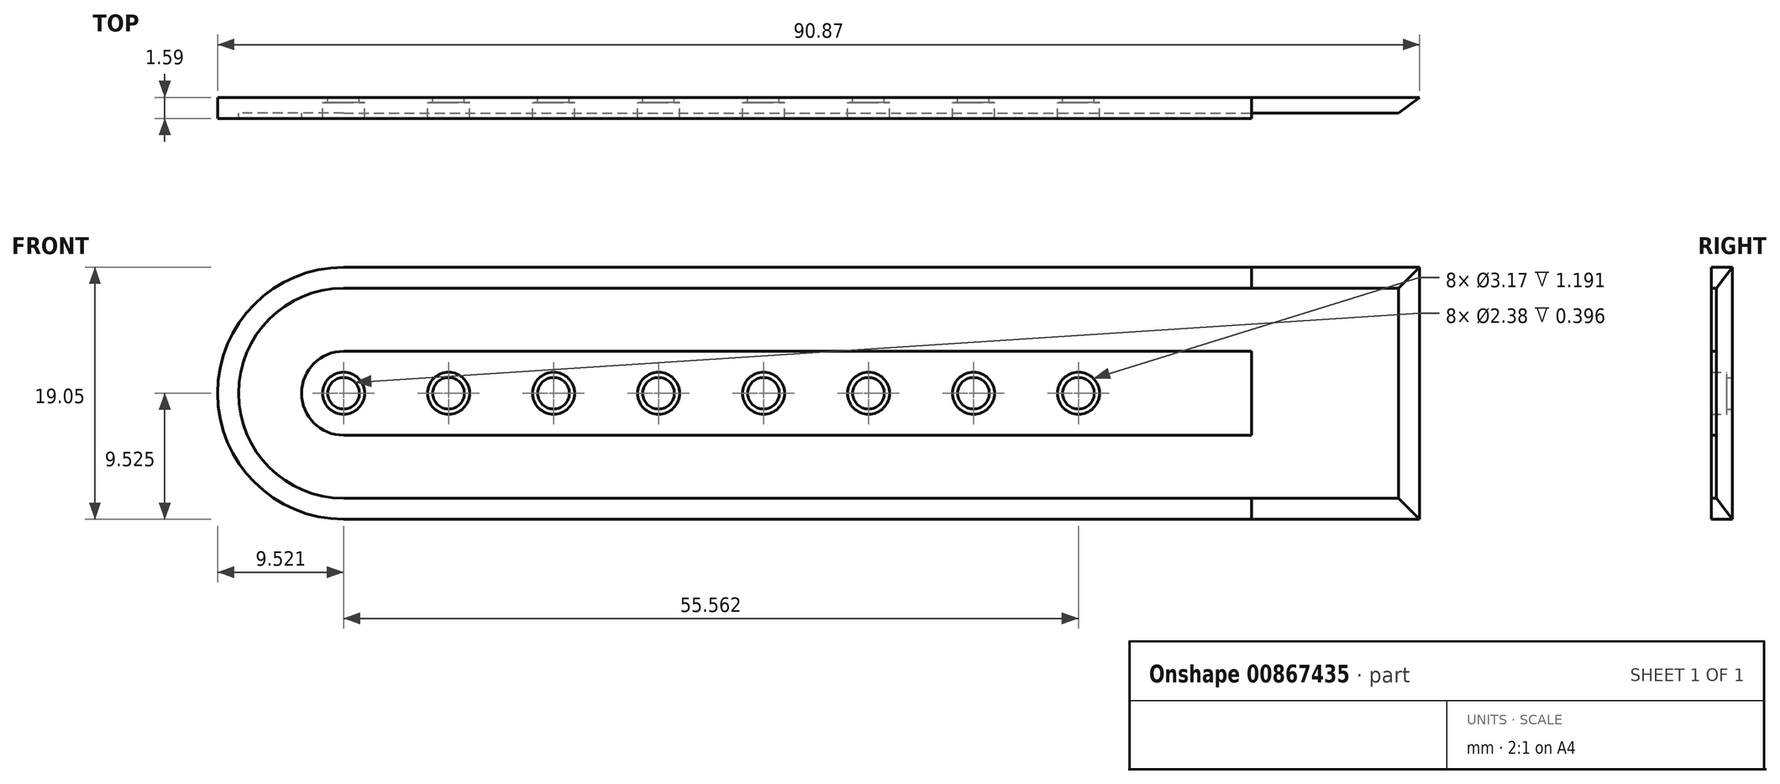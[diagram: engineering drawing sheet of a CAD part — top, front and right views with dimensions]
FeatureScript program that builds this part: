
annotation { "Feature Type Name" : "Feature", "Feature Type Description" : "" }
export const myFeature = defineFeature(function(context is Context, id is Id, definition is map)
    precondition{}
    {
        {
            var Q0;
            Q0=qCreatedBy(makeId("Front.planeOp"),FACE);
            var sketch = newSketch(context, id + "F0", { "sketchPlane" : qUnion([Q0])});
            skLineSegment(sketch, "E0", {"start": v(0, 0) * mm, "end": v(-81.36, 0) * mm});
            skLineSegment(sketch, "E1", {"start": v(0, 19.05) * mm, "end": v(-81.36, 19.05) * mm});
            skArc(sketch, "E2", {"start": v(-81.36, 19.05) * mm, "mid": v(-90.88, 9.52) * mm, "end": v(-81.36, 0) * mm});
            skLineSegment(sketch, "E3", {"start": v(0, 19.05) * mm, "end": v(0, 0) * mm});
            skCircle(sketch, "E4", {"center": v(-73.42, 9.52) * mm, "radius": 1.59 * mm});
            skCircle(sketch, "E5", {"center": v(-65.48, 9.52) * mm, "radius": 1.59 * mm});
            skCircle(sketch, "E6", {"center": v(-57.55, 9.52) * mm, "radius": 1.59 * mm});
            skCircle(sketch, "E7", {"center": v(-49.6, 9.52) * mm, "radius": 1.59 * mm});
            skCircle(sketch, "E8", {"center": v(-41.67, 9.52) * mm, "radius": 1.59 * mm});
            skCircle(sketch, "E9", {"center": v(-33.73, 9.52) * mm, "radius": 1.59 * mm});
            skCircle(sketch, "E10", {"center": v(-81.36, 9.52) * mm, "radius": 1.59 * mm});
            skCircle(sketch, "E11", {"center": v(-25.8, 9.52) * mm, "radius": 1.59 * mm});
            skArc(sketch, "E12", {"start": v(-81.36, 17.46) * mm, "mid": v(-89.3, 9.52) * mm, "end": v(-81.36, 1.59) * mm});
            skCircle(sketch, "E13", {"center": v(-81.36, 9.52) * mm, "radius": 1.2 * mm});
            skCircle(sketch, "E14", {"center": v(-73.42, 9.52) * mm, "radius": 1.2 * mm});
            skCircle(sketch, "E15", {"center": v(-65.48, 9.52) * mm, "radius": 1.2 * mm});
            skCircle(sketch, "E16", {"center": v(-57.55, 9.52) * mm, "radius": 1.2 * mm});
            skCircle(sketch, "E17", {"center": v(-49.6, 9.52) * mm, "radius": 1.2 * mm});
            skCircle(sketch, "E18", {"center": v(-41.67, 9.52) * mm, "radius": 1.2 * mm});
            skCircle(sketch, "E19", {"center": v(-33.73, 9.52) * mm, "radius": 1.2 * mm});
            skCircle(sketch, "E20", {"center": v(-25.8, 9.52) * mm, "radius": 1.2 * mm});
            skLineSegment(sketch, "E21", {"start": v(-81.36, 12.7) * mm, "end": v(-12.7, 12.7) * mm});
            skLineSegment(sketch, "E22", {"start": v(-81.36, 6.35) * mm, "end": v(-12.7, 6.35) * mm});
            skLineSegment(sketch, "E23", {"start": v(-12.7, 12.7) * mm, "end": v(-12.7, 6.35) * mm});
            skArc(sketch, "E24", {"start": v(-81.36, 12.7) * mm, "mid": v(-84.53, 9.52) * mm, "end": v(-81.36, 6.35) * mm});
            skLineSegment(sketch, "E25", {"start": v(-81.36, 17.46) * mm, "end": v(-12.7, 17.46) * mm});
            skLineSegment(sketch, "E26", {"start": v(-81.36, 1.59) * mm, "end": v(-12.7, 1.59) * mm});
            skLineSegment(sketch, "E27", {"start": v(-12.7, 17.46) * mm, "end": v(-12.7, 19.05) * mm});
            skLineSegment(sketch, "E28", {"start": v(-12.7, 1.59) * mm, "end": v(-12.7, 0) * mm});
            skLineSegment(sketch, "E29", {"start": v(-12.7, 17.46) * mm, "end": v(-1.59, 17.46) * mm});
            skLineSegment(sketch, "E30", {"start": v(-12.7, 1.59) * mm, "end": v(-1.59, 1.59) * mm});
            skLineSegment(sketch, "E31", {"start": v(-1.59, 17.46) * mm, "end": v(-1.59, 1.59) * mm});
            skSolve(sketch);
        }
        {
            var Q0;
            {var subQ0=sQuery(id+"F0.wireOp",EDGE,"E2");Q0=makeQuery(id+"F0.imprint","IMPRINT",FACE,{"disambiguationData":[TD([[makeQuery(id+"F0.imprint","IMPRINT",EDGE,{"derivedFrom":subQ0}),1.0]])]});}
            extrude(context, id + "F1", {"entities" : qUnion([Q0]), "depth" : 1.59 * mm, "offsetDistance" : 25.4 * mm});
        }
        {
            var Q0;
            Q0=makeQuery(id+"F0.imprint","IMPRINT",FACE,{"disambiguationData":[TD([[makeQuery(id+"F0.imprint","IMPRINT",EDGE,{"derivedFrom":sQuery(id+"F0.wireOp",EDGE,"E12")}),1.0]])]});
            extrude(context, id + "F2", {"entities" : qUnion([Q0]), "operationType" : NewBodyOperationType.ADD, "depth" : 1.19 * mm, "offsetDistance" : 25.4 * mm});
        }
        {
            var Q0;
            Q0=makeQuery(id+"F0.imprint","IMPRINT",FACE,{"disambiguationData":[TD([[makeQuery(id+"F0.imprint","IMPRINT",EDGE,{"derivedFrom":sQuery(id+"F0.wireOp",EDGE,"E4")}),-1.0]])]});
            extrude(context, id + "F3", {"entities" : qUnion([Q0]), "operationType" : NewBodyOperationType.ADD, "depth" : 1.59 * mm, "offsetDistance" : 25.4 * mm});
        }
        {
            var Q0;
            Q0=makeQuery(id+"F0.imprint","IMPRINT",FACE,{"disambiguationData":[TD([[makeQuery(id+"F0.imprint","IMPRINT",EDGE,{"derivedFrom":sQuery(id+"F0.wireOp",EDGE,"E10")}),1.0]])]});
            var Q1;
            Q1=makeQuery(id+"F0.imprint","IMPRINT",FACE,{"disambiguationData":[TD([[makeQuery(id+"F0.imprint","IMPRINT",EDGE,{"derivedFrom":sQuery(id+"F0.wireOp",EDGE,"E4")}),1.0]])]});
            var Q2;
            Q2=makeQuery(id+"F0.imprint","IMPRINT",FACE,{"disambiguationData":[TD([[makeQuery(id+"F0.imprint","IMPRINT",EDGE,{"derivedFrom":sQuery(id+"F0.wireOp",EDGE,"E5")}),1.0]])]});
            var Q3;
            Q3=makeQuery(id+"F0.imprint","IMPRINT",FACE,{"disambiguationData":[TD([[makeQuery(id+"F0.imprint","IMPRINT",EDGE,{"derivedFrom":sQuery(id+"F0.wireOp",EDGE,"E6")}),1.0]])]});
            var Q4;
            Q4=makeQuery(id+"F0.imprint","IMPRINT",FACE,{"disambiguationData":[TD([[makeQuery(id+"F0.imprint","IMPRINT",EDGE,{"derivedFrom":sQuery(id+"F0.wireOp",EDGE,"E7")}),1.0]])]});
            var Q5;
            Q5=makeQuery(id+"F0.imprint","IMPRINT",FACE,{"disambiguationData":[TD([[makeQuery(id+"F0.imprint","IMPRINT",EDGE,{"derivedFrom":sQuery(id+"F0.wireOp",EDGE,"E8")}),1.0]])]});
            var Q6;
            Q6=makeQuery(id+"F0.imprint","IMPRINT",FACE,{"disambiguationData":[TD([[makeQuery(id+"F0.imprint","IMPRINT",EDGE,{"derivedFrom":sQuery(id+"F0.wireOp",EDGE,"E9")}),1.0]])]});
            var Q7;
            Q7=makeQuery(id+"F0.imprint","IMPRINT",FACE,{"disambiguationData":[TD([[makeQuery(id+"F0.imprint","IMPRINT",EDGE,{"derivedFrom":sQuery(id+"F0.wireOp",EDGE,"E11")}),1.0]])]});
            extrude(context, id + "F4", {"entities" : qUnion([Q0, Q1, Q2, Q3, Q4, Q5, Q6, Q7]), "operationType" : NewBodyOperationType.ADD, "depth" : 0.4 * mm, "offsetDistance" : 25.4 * mm});
        }
        {
            var Q0;
            {var subQ1=sQuery(id+"F0.wireOp",EDGE,"E3");Q0=makeQuery(id+"F0.imprint","IMPRINT",FACE,{"disambiguationData":[TD([[makeQuery(id+"F0.imprint","IMPRINT",EDGE,{"derivedFrom":subQ1}),-1.0]])]});}
            extrude(context, id + "F5", {"entities" : qUnion([Q0]), "operationType" : NewBodyOperationType.ADD, "depth" : 1.19 * mm, "offsetDistance" : 25.4 * mm});
        }
        {
            var Q0;
            Q0=makeQuery(id+"F5.opExtrude","CAP_EDGE",EDGE,{"disambiguationData":[OSD([sQuery(id+"F0.wireOp",EDGE,"E1")])],"isStart":false});
            var Q1;
            Q1=makeQuery(id+"F5.opExtrude","CAP_EDGE",EDGE,{"disambiguationData":[OSD([sQuery(id+"F0.wireOp",EDGE,"E3")])],"isStart":false});
            var Q2;
            Q2=makeQuery(id+"F5.opExtrude","CAP_EDGE",EDGE,{"disambiguationData":[OSD([sQuery(id+"F0.wireOp",EDGE,"E0")])],"isStart":false});
            chamfer(context, id + "F6", {"entities" : qUnion([Q0, Q1, Q2]), "chamferType" : ChamferType.OFFSET_ANGLE, "width" : 1.59 * mm, "oppositeDirection" : false, "angle" : 37 * degree, "tangentPropagation" : true});
        }
    });
